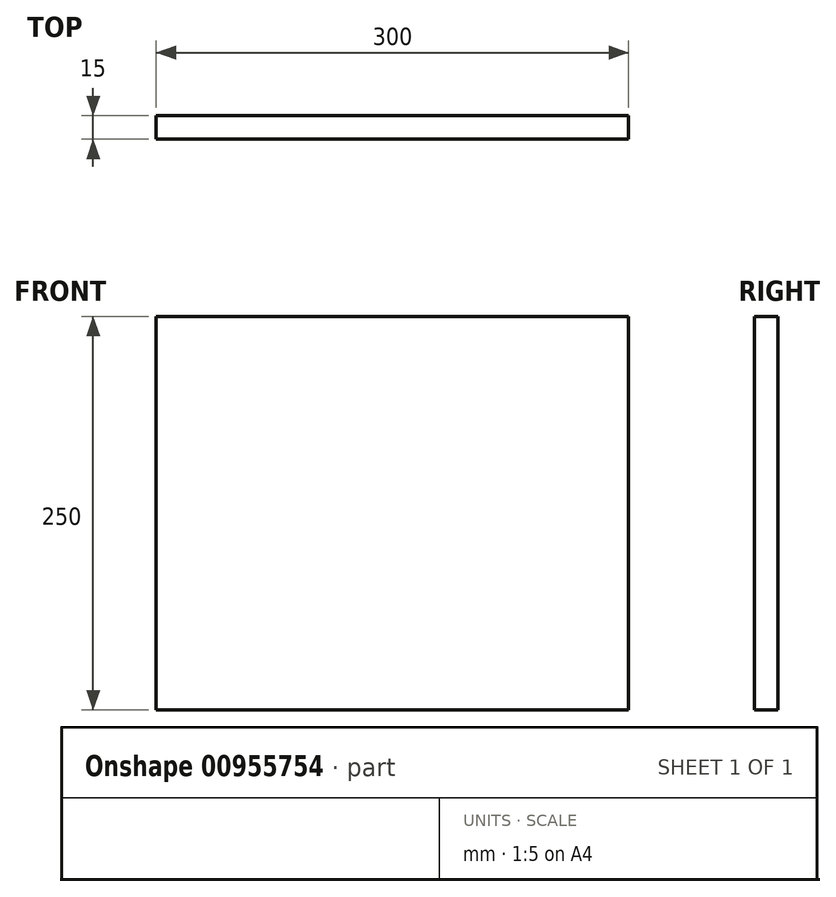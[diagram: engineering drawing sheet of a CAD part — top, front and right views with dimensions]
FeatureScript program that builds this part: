
annotation { "Feature Type Name" : "Feature", "Feature Type Description" : "" }
export const myFeature = defineFeature(function(context is Context, id is Id, definition is map)
    precondition{}
    {
        {
            var Q0;
            Q0=qCreatedBy(makeId("Front.planeOp"),FACE);
            var sketch = newSketch(context, id + "F0", { "sketchPlane" : qUnion([Q0])});
            skLineSegment(sketch, "E0.bottom", {"start": v(0, 0) * mm, "end": v(300, 0) * mm});
            skLineSegment(sketch, "E0.top", {"start": v(0, -250) * mm, "end": v(300, -250) * mm});
            skLineSegment(sketch, "E0.left", {"start": v(0, 0) * mm, "end": v(0, -250) * mm});
            skLineSegment(sketch, "E0.right", {"start": v(300, 0) * mm, "end": v(300, -250) * mm});
            skSolve(sketch);
        }
        {
            var Q0;
            Q0 = qSketchRegion(id + "F0", true);
            extrude(context, id + "F1", {"entities" : qUnion([Q0]), "depth" : 15 * mm, "offsetDistance" : 25 * mm});
        }
    });
